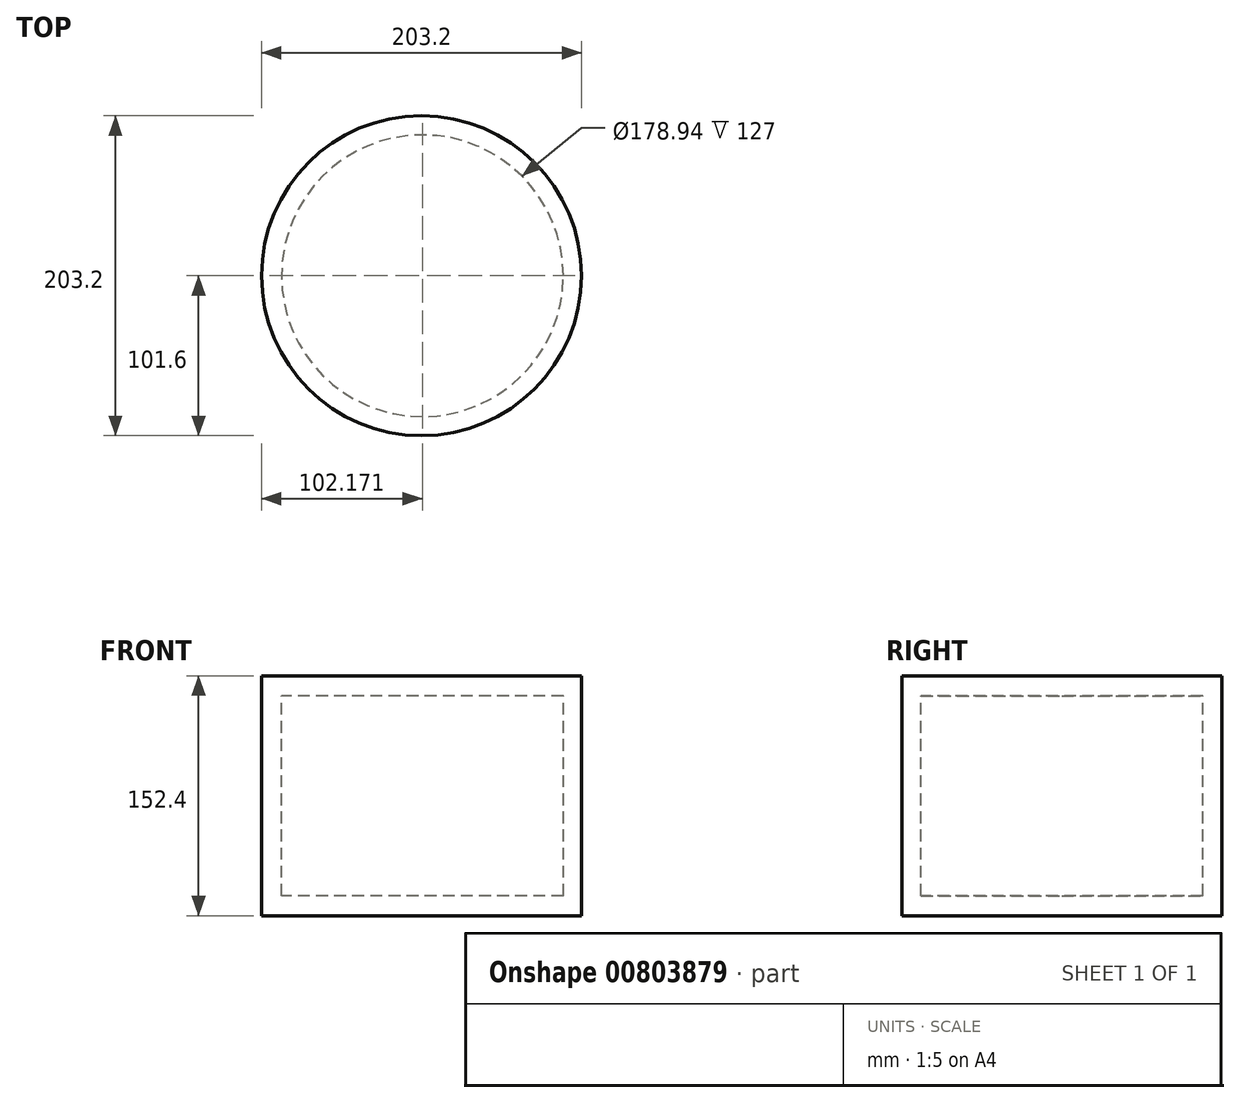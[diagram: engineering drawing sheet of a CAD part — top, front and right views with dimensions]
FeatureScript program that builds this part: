
annotation { "Feature Type Name" : "Feature", "Feature Type Description" : "" }
export const myFeature = defineFeature(function(context is Context, id is Id, definition is map)
    precondition{}
    {
        {
            var Q0;
            Q0=qCreatedBy(makeId("Front.planeOp"),FACE);
            var sketch = newSketch(context, id + "F0", { "sketchPlane" : qUnion([Q0])});
            skLineSegment(sketch, "E0.bottom", {"start": v(-50.8, 76.2) * mm, "end": v(50.8, 76.2) * mm});
            skLineSegment(sketch, "E0.top", {"start": v(-50.8, -76.2) * mm, "end": v(50.8, -76.2) * mm});
            skLineSegment(sketch, "E0.left", {"start": v(-50.8, 76.2) * mm, "end": v(-50.8, -76.2) * mm});
            skLineSegment(sketch, "E0.right", {"start": v(50.8, 76.2) * mm, "end": v(50.8, -76.2) * mm});
            skPoint(sketch, "E0.middle", {"position": v(0, 0) * mm});
            skSolve(sketch);
        }
        {
            var Q0;
            {var subQ0=sQuery(id+"F0.wireOp",EDGE,"E0.left");Q0=makeQuery(id+"F0.imprint","IMPRINT",FACE,{"disambiguationData":[TD([[makeQuery(id+"F0.imprint","IMPRINT",EDGE,{"derivedFrom":subQ0}),1.0]])]});}
            var Q1;
            {var subQ0=sQuery(id+"F0.wireOp",EDGE,"E0.right");Q1=makeQuery(id+"F0.imprint","IMPRINT",FACE,{"disambiguationData":[TD([[makeQuery(id+"F0.imprint","IMPRINT",EDGE,{"derivedFrom":subQ0}),-1.0]])]});}
            var Q2;
            Q2=sQuery(id+"F0.wireOp",EDGE,"E0.right");
            revolve(context, id + "F1", {"surfaceOperationType" : NewSurfaceOperationType.NEW, "entities" : qUnion([Q0, Q1]), "axis" : qUnion([Q2]), "revolveType" : RevolveType.FULL});
        }
        {
            var Q0;
            Q0=makeQuery(id+"F1.opRevolve","SWEPT_FACE",FACE,{"disambiguationData":[OSD([sQuery(id+"F0.wireOp",EDGE,"E0.left")])]});
            var Q1;
            Q1=makeQuery(id+"F1.opRevolve","SWEPT_BODY",BODY,{"disambiguationData":[OSD([sQuery(id+"F0.wireOp",EDGE,"E0.bottom"),sQuery(id+"F0.wireOp",EDGE,"E0.top"),sQuery(id+"F0.wireOp",EDGE,"E0.left"),sQuery(id+"F0.wireOp",EDGE,"E0.right")])]});
            shell(context, id + "F2", {"isHollow" : true, "entities" : qUnion([Q0]), "parts" : qUnion([Q1]), "thickness" : 12.7 * mm});
        }
        {
            var Q0;
            Q0=qCreatedBy(makeId("Top.planeOp"),FACE);
            var sketch = newSketch(context, id + "F3", { "sketchPlane" : qUnion([Q0])});
            skCircle(sketch, "E1", {"center": v(51.37, 0) * mm, "radius": 89.47 * mm});
            skSolve(sketch);
        }
        {
            var Q0;
            Q0 = qSketchRegion(id + "F3", true);
            extrude(context, id + "F4", {"entities" : qUnion([Q0]), "operationType" : NewBodyOperationType.REMOVE, "endBound" : BoundingType.SYMMETRIC, "oppositeDirection" : true, "depth" : 127 * mm, "offsetDistance" : 25.4 * mm});
        }
    });
